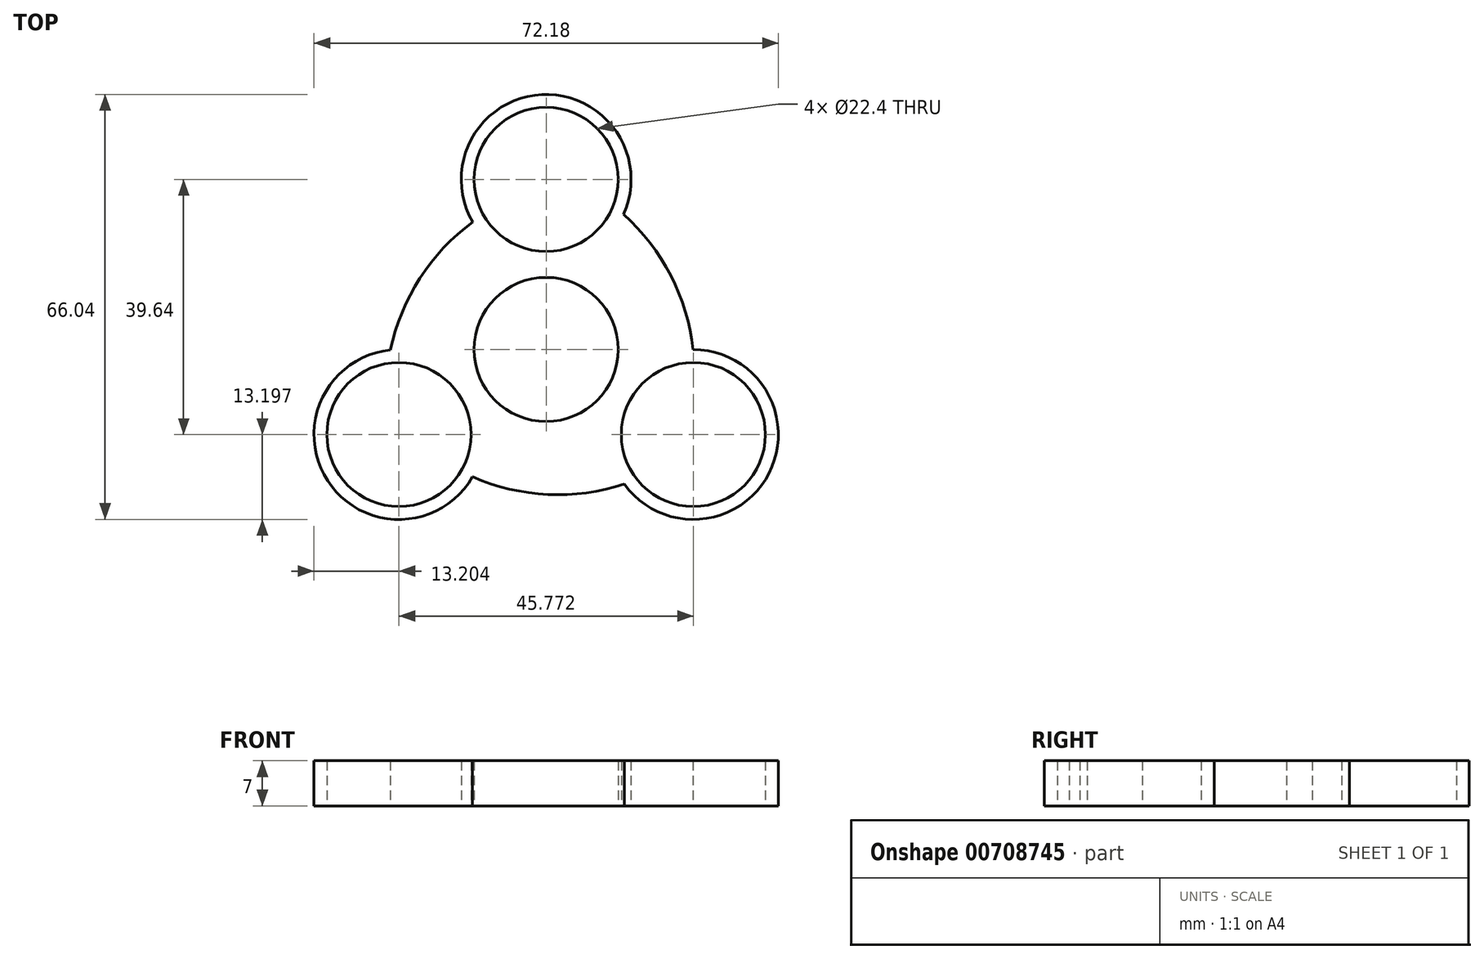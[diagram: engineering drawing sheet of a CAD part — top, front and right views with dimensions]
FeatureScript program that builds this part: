
annotation { "Feature Type Name" : "Feature", "Feature Type Description" : "" }
export const myFeature = defineFeature(function(context is Context, id is Id, definition is map)
    precondition{}
    {
        {
            var Q0;
            Q0=qCreatedBy(makeId("Top.planeOp"),FACE);
            var sketch = newSketch(context, id + "F0", { "sketchPlane" : qUnion([Q0])});
            skCircle(sketch, "E0", {"center": v(0, 0) * mm, "radius": 11.2 * mm});
            skCircle(sketch, "E1", {"center": v(0, 26.43) * mm, "radius": 11.2 * mm});
            skArc(sketch, "E2", {"start": v(12.03, 21) * mm, "mid": v(-0.68, 39.6) * mm, "end": v(-11.41, 19.8) * mm});
            skArc(sketch, "E3.1.0", {"start": v(-24.2, -0.08) * mm, "mid": v(-33.96, -20.39) * mm, "end": v(-11.44, -19.78) * mm});
            skArc(sketch, "E3.2.0", {"start": v(12.17, -20.92) * mm, "mid": v(34.64, -19.22) * mm, "end": v(22.85, -0.01) * mm});
            skCircle(sketch, "E4.1.0", {"center": v(-22.89, -13.21) * mm, "radius": 11.2 * mm});
            skCircle(sketch, "E4.2.0", {"center": v(22.89, -13.21) * mm, "radius": 11.2 * mm});
            skArc(sketch, "E5", {"start": v(22.85, -0.01) * mm, "mid": v(19.38, 11.49) * mm, "end": v(12.03, 21) * mm});
            skArc(sketch, "E6.1.0", {"start": v(-11.41, 19.8) * mm, "mid": v(-19.64, 11.04) * mm, "end": v(-24.2, -0.08) * mm});
            skArc(sketch, "E6.2.0", {"start": v(-11.44, -19.78) * mm, "mid": v(0.26, -22.53) * mm, "end": v(12.17, -20.92) * mm});
            skSolve(sketch);
        }
        {
            var Q0;
            Q0 = qSketchRegion(id + "F0", true);
            extrude(context, id + "F1", {"entities" : qUnion([Q0]), "depth" : 7 * mm, "offsetDistance" : 25 * mm});
        }
    });
